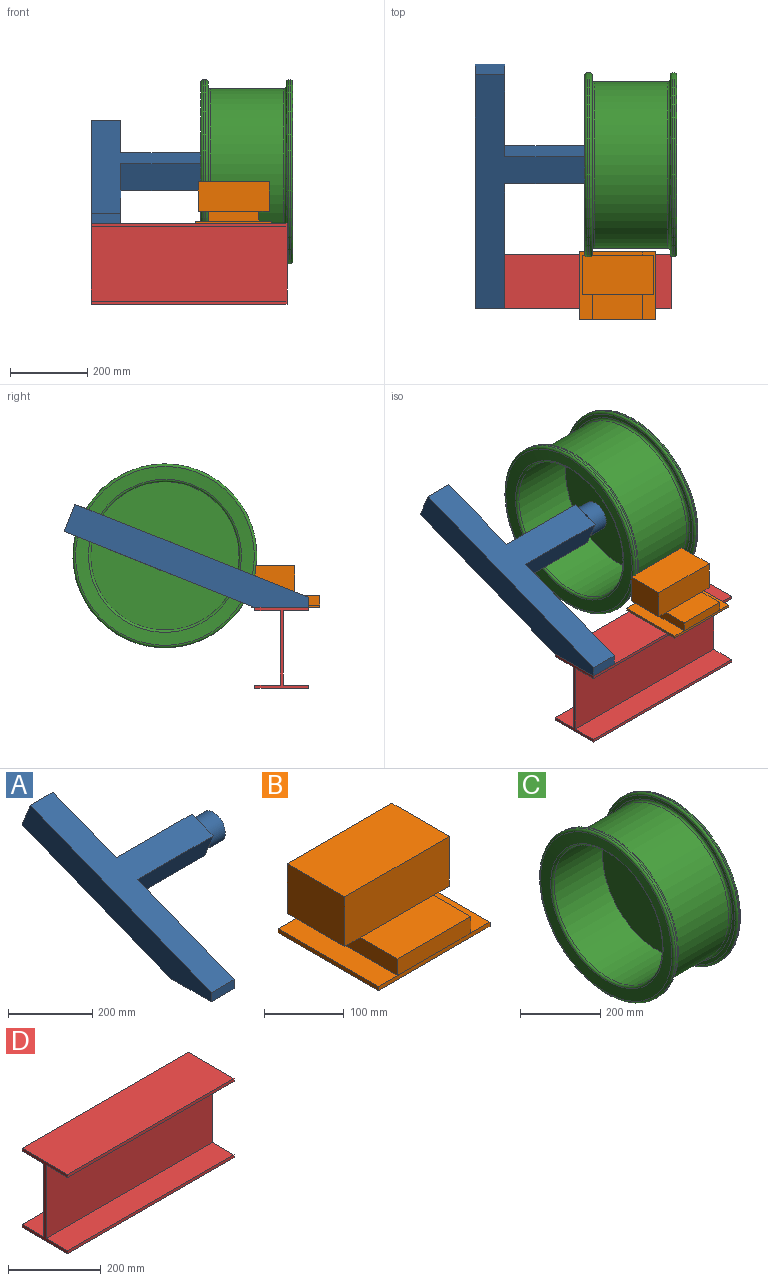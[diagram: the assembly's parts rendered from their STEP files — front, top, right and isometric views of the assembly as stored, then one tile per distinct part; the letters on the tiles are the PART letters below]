
ASSEMBLY  parts=4 mates=5
PART A: 20 faces, bbox 381x635.3x268 mm
  f0: plane 35.84x25.64mm, normal (1,0,0), area 244.8mm2, adj f7,f9,f15
  f1: plane 35.84x25.64mm, normal (1,0,0), area 244.8mm2, adj f6,f9,f15
  f2: plane 35.84x25.64mm, normal (1,0,0), area 244.8mm2, adj f6,f10,f15
  f3: plane 352.1x155.32mm, normal (1,0,0), area 23837.9mm2, adj f5,f6,f7,f8,f10
  f4: plane 635.3x268.02mm, normal (-1,0,0), area 47063.6mm2, adj f5,f6,f7,f8,f19
  f5: plane 139.7x76.2mm, normal (0,0,-1), area 10645.1mm2, adj f3,f4,f7,f8
  f6: plane 607.12x330.2mm, normal (0,-0.37,0.93), area 69146.3mm2, adj f1,f2,f3,f4,f8,f9,f10,f17
  f7: plane 495.6x330.2mm, normal (0,0.37,-0.93), area 59999.9mm2, adj f0,f3,f4,f5,f9,f10,f11,f13
  f8: plane 76.2x26.42mm, normal (0,-1,0), area 2013.1mm2, adj f3,f4,f5,f6
  f9: plane 254x70.8mm, normal (0,0.93,0.37), area 19354.8mm2, adj f0,f1,f6,f7,f14,f18
  f10: plane 254x70.8mm, normal (0,-0.93,-0.37), area 19354.8mm2, adj f2,f3,f6,f7,f11,f12
  f11: plane 35.84x25.64mm, normal (1,0,0), area 244.8mm2, adj f7,f10,f15
  f12: plane 19.52x7.77mm, normal (-1,0,0), area 20mm2, adj f10,f15
  f13: plane 19.52x7.77mm, normal (-1,0,0), area 20mm2, adj f7,f15
  f14: plane 19.52x7.77mm, normal (-1,0,0), area 20mm2, adj f9,f15
  f15: cylinder r=39.52mm len=79.04mm, axis (-1,0,0), area 12614.9mm2, adj f0,f1,f2,f11,f12,f13,f14,f16
  f16: plane 79.04x79.04mm, normal (1,0,0), area 4907.2mm2, adj f15
  f17: plane 19.52x7.77mm, normal (-1,0,0), area 20mm2, adj f6,f15
  f18: plane 240.57x155.32mm, normal (1,0,0), area 17419.3mm2, adj f6,f7,f9,f19
  f19: plane 76.2x70.8mm, normal (0,0.93,0.37), area 5806.4mm2, adj f4,f6,f7,f18
PART B: 22 faces, bbox 197.8x177.8x108 mm
  f0: plane 130.18x0.14mm, normal (0,0,-1), area 17.9mm2, adj f2,f4,f5,f18
  f1: plane 130.18x65.88mm, normal (0,0,1), area 8576.4mm2, adj f2,f4,f5,f9
  f2: plane 177.8x25.4mm, normal (1,0,0), area 4516.1mm2, adj f0,f1,f3,f5,f6,f7,f14,f15
  f3: plane 130.18x25.4mm, normal (0,1,0), area 3306.4mm2, adj f2,f4,f6,f7
  f4: plane 177.8x25.4mm, normal (-1,0,0), area 4516.1mm2, adj f0,f1,f3,f5,f6,f7,f8,f21
  f5: plane 130.18x25.4mm, normal (0,-1,0), area 3306.4mm2, adj f0,f1,f2,f4
  f6: plane 130.18x10.32mm, normal (0,0,1), area 1343mm2, adj f2,f3,f4,f11
  f7: plane 130.18x0.14mm, normal (0,0,-1), area 17.9mm2, adj f2,f3,f4,f16
  f8: plane 101.6x27.62mm, normal (0,0,-1), area 2806.4mm2, adj f4,f9,f11,f12
  f9: plane 185.42x76.2mm, normal (0,-1,0), area 14129mm2, adj f1,f8,f10,f12,f13,f14
  f10: plane 101.6x76.2mm, normal (1,0,0), area 7741.9mm2, adj f9,f11,f13,f14
  f11: plane 185.42x76.2mm, normal (0,1,0), area 14129mm2, adj f6,f8,f10,f12,f13,f14
  f12: plane 101.6x76.2mm, normal (-1,0,0), area 7741.9mm2, adj f8,f9,f11,f13
  f13: plane 185.42x101.6mm, normal (0,0,1), area 18838.7mm2, adj f9,f10,f11,f12
  f14: plane 101.6x27.62mm, normal (0,0,-1), area 2806.4mm2, adj f2,f9,f10,f11
  f15: plane 177.52x33.82mm, normal (0,0,1), area 6003.2mm2, adj f2,f16,f17,f18
  f16: plane 197.81x6.35mm, normal (0,1,0), area 1256.1mm2, adj f7,f15,f17,f19,f20,f21
  f17: plane 177.52x6.35mm, normal (1,0,0), area 1127.3mm2, adj f15,f16,f18,f20
  f18: plane 197.81x6.35mm, normal (0,-1,0), area 1256.1mm2, adj f0,f15,f17,f19,f20,f21
  f19: plane 177.52x6.35mm, normal (-1,0,0), area 1127.3mm2, adj f16,f18,f20,f21
  f20: plane 197.81x177.52mm, normal (0,0,-1), area 35115.7mm2, adj f16,f17,f18,f19
  f21: plane 177.52x33.82mm, normal (0,0,1), area 6003.2mm2, adj f4,f16,f18,f19
PART C: 20 faces, bbox 238.7x517.3x517.3 mm
  f0: torus R=232.6mm, axis (-1,0,0), area 14830.9mm2, adj f1,f19
  f1: cylinder r=238.95mm len=477.9mm, axis (-1,0,0), area 9967.7mm2, adj f0,f2
  f2: torus R=232.6mm, axis (-1,0,0), area 15508.5mm2, adj f1,f3
  f3: cone r=232.14mm half-angle=85.8deg, axis (-1,0,0), area 45571mm2, adj f2,f4
  f4: torus R=199.01mm, axis (-1,0,0), area 11639.3mm2, adj f3,f5
  f5: cylinder r=192.66mm len=385.32mm, axis (-1,0,0), area 207196.4mm2, adj f4,f6
  f6: plane 385.32x385.32mm, normal (-1,0,0), area 116608.5mm2, adj f5
  f7: plane 214.35x214.35mm, normal (1,0,0), area 36085.4mm2, adj f8
  f8: revolved ~385.32x385.32mm, area 83474.5mm2, adj f7,f9
  f9: cylinder r=192.66mm len=385.32mm, axis (-1,0,0), area 10915.9mm2, adj f8,f10
  f10: torus R=199.01mm, axis (-1,0,0), area 10369.4mm2, adj f9,f11
  f11: cone r=197.54mm half-angle=76.6deg, axis (1,0,0), area 46502mm2, adj f10,f12
  f12: torus R=232.6mm, axis (-1,0,0), area 16993.8mm2, adj f11,f13
  f13: cylinder r=238.95mm len=477.9mm, axis (-1,0,0), area 5329.6mm2, adj f12,f14
  f14: torus R=232.6mm, axis (-1,0,0), area 14870mm2, adj f13,f15
  f15: cone r=232.57mm half-angle=89.8deg, axis (-1,0,0), area 14713.7mm2, adj f14,f16
  f16: torus R=222.25mm, axis (-1,0,0), area 13712.8mm2, adj f15,f17
  f17: cylinder r=215.9mm len=431.8mm, axis (-1,0,0), area 258384.5mm2, adj f16,f18
  f18: torus R=222.25mm, axis (-1,0,0), area 13675.5mm2, adj f17,f19
  f19: plane 465.2x465.2mm, normal (1,0,0), area 14790.1mm2, adj f0,f18
PART D: 14 faces, bbox 508x139.7x209.6 mm
  f0: plane 508x139.7mm, normal (0,0,1), area 70967.6mm2, adj f1,f11,f12,f13
  f1: plane 508x7.94mm, normal (0,-1,0), area 4032.2mm2, adj f0,f2,f12,f13
  f2: plane 508x66.01mm, normal (0,0,-1), area 33535.4mm2, adj f1,f3,f12,f13
  f3: plane 508x193.68mm, normal (0,-1,0), area 98386.9mm2, adj f2,f4,f12,f13
  f4: plane 508x66.01mm, normal (0,0,1), area 33535.4mm2, adj f3,f5,f12,f13
  f5: plane 508x7.94mm, normal (0,-1,0), area 4032.2mm2, adj f4,f6,f12,f13
  f6: plane 508x139.7mm, normal (0,0,-1), area 70967.6mm2, adj f5,f7,f12,f13
  f7: plane 508x7.94mm, normal (0,1,0), area 4032.2mm2, adj f6,f8,f12,f13
  f8: plane 508x66.01mm, normal (0,0,1), area 33535.4mm2, adj f7,f9,f12,f13
  f9: plane 508x193.68mm, normal (0,1,0), area 98386.9mm2, adj f8,f10,f12,f13
  f10: plane 508x66.01mm, normal (0,0,-1), area 33535.4mm2, adj f9,f11,f12,f13
  f11: plane 508x7.94mm, normal (0,1,0), area 4032.2mm2, adj f0,f10,f12,f13
  f12: plane 209.55x139.7mm, normal (-1,0,0), area 3703.4mm2, adj f0,f1,f2,f3,f4,f5,f6,f7
  f13: plane 209.55x139.7mm, normal (1,0,0), area 3703.4mm2, adj f0,f1,f2,f3,f4,f5,f6,f7
PLACE A t=(-137.24,51.39,64.11)mm
PLACE B t=(232.43,27.14,70.46)mm
PLACE C t=(299.08,340.74,198.12)mm
PLACE D t=(370.76,37.18,-40.67)mm
MATE planar A.f8 <-> D.f1  axis (0,-1,0) through (-99.14,-32.67,77.32)mm
MATE planar A.f4 <-> D.f12  axis (-1,0,0) through (-137.24,37.18,64.11)mm
MATE planar D.f0 <-> B.f20  axis (0,0,1) through (116.76,37.18,64.11)mm
MATE planar D.f0 <-> A.f5  axis (0,0,1) through (116.76,37.18,64.11)mm
MATE cylindrical A.f15 <-> C.f0  axis (1,0,0) through (243.76,340.74,198.12)mm
